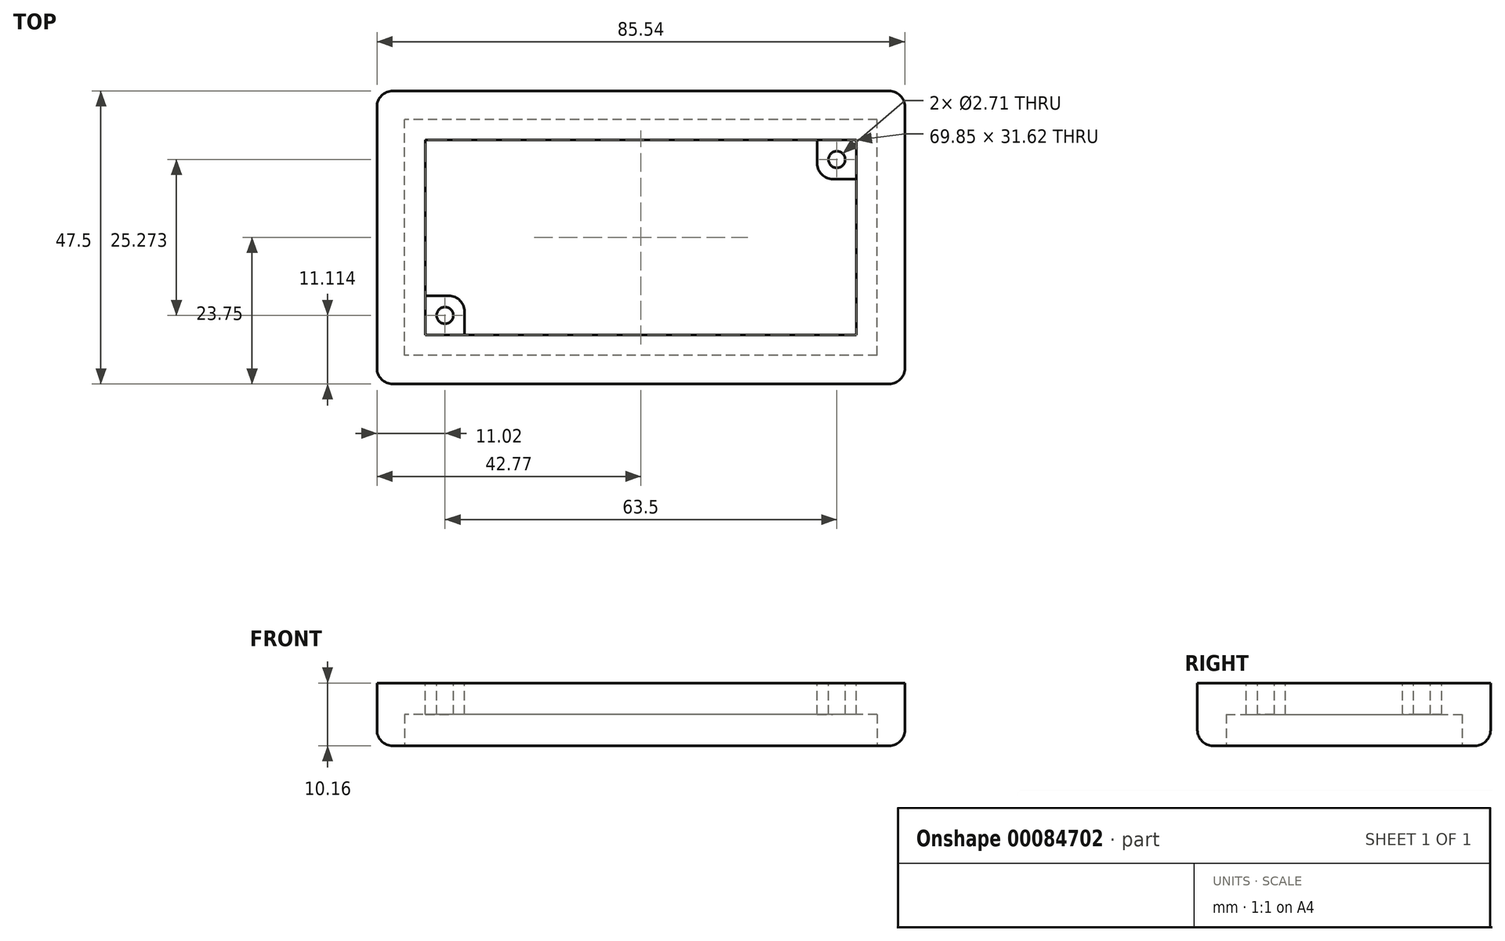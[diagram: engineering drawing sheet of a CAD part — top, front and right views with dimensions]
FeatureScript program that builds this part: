
annotation { "Feature Type Name" : "Feature", "Feature Type Description" : "" }
export const myFeature = defineFeature(function(context is Context, id is Id, definition is map)
    precondition{}
    {
        {
            var Q0;
            Q0=qCreatedBy(makeId("Top.planeOp"),FACE);
            var sketch = newSketch(context, id + "F0", { "sketchPlane" : qUnion([Q0])});
            skLineSegment(sketch, "E0.rect.bottom", {"start": v(34.93, -15.81) * mm, "end": v(-34.93, -15.81) * mm});
            skLineSegment(sketch, "E0.rect.top", {"start": v(34.93, 15.81) * mm, "end": v(-34.93, 15.81) * mm});
            skLineSegment(sketch, "E0.rect.left", {"start": v(34.93, -15.81) * mm, "end": v(34.93, 15.81) * mm});
            skLineSegment(sketch, "E0.rect.right", {"start": v(-34.93, -15.81) * mm, "end": v(-34.93, 15.81) * mm});
            skPoint(sketch, "E0.rect.middle", {"position": v(0, 0) * mm});
            skLineSegment(sketch, "E1.rect.bottom", {"start": v(42.77, -23.75) * mm, "end": v(-42.77, -23.75) * mm});
            skLineSegment(sketch, "E1.rect.top", {"start": v(42.77, 23.75) * mm, "end": v(-42.77, 23.75) * mm});
            skLineSegment(sketch, "E1.rect.left", {"start": v(42.77, -23.75) * mm, "end": v(42.77, 23.75) * mm});
            skLineSegment(sketch, "E1.rect.right", {"start": v(-42.77, -23.75) * mm, "end": v(-42.77, 23.75) * mm});
            skSolve(sketch);
        }
        {
            var Q0;
            Q0=makeQuery(id+"F0.imprint","IMPRINT",FACE,{"disambiguationData":[TD([[makeQuery(id+"F0.imprint","IMPRINT",EDGE,{"derivedFrom":sQuery(id+"F0.wireOp",EDGE,"E0.rect.bottom")}),1.0]])]});
            extrude(context, id + "F1", {"entities" : qUnion([Q0]), "depth" : 10.16 * mm});
        }
        {
            var Q0;
            Q0=makeQuery(id+"F1.opExtrude","CAP_FACE",FACE,{"disambiguationData":[OSD([sQuery(id+"F0.wireOp",EDGE,"E0.rect.bottom"),sQuery(id+"F0.wireOp",EDGE,"E0.rect.top"),sQuery(id+"F0.wireOp",EDGE,"E0.rect.left"),sQuery(id+"F0.wireOp",EDGE,"E0.rect.right"),sQuery(id+"F0.wireOp",EDGE,"E1.rect.bottom"),sQuery(id+"F0.wireOp",EDGE,"E1.rect.top"),sQuery(id+"F0.wireOp",EDGE,"E1.rect.left"),sQuery(id+"F0.wireOp",EDGE,"E1.rect.right")])],"isStart":false});
            var sketch = newSketch(context, id + "F2", { "sketchPlane" : qUnion([Q0])});
            skLineSegment(sketch, "E2.bottom", {"start": v(-34.93, -15.81) * mm, "end": v(-28.58, -15.81) * mm});
            skLineSegment(sketch, "E2.top", {"start": v(-34.93, -9.46) * mm, "end": v(-28.57, -9.46) * mm});
            skLineSegment(sketch, "E2.left", {"start": v(-34.93, -15.81) * mm, "end": v(-34.93, -9.46) * mm});
            skLineSegment(sketch, "E2.right", {"start": v(-28.58, -15.81) * mm, "end": v(-28.58, -9.46) * mm});
            skLineSegment(sketch, "E3.bottom", {"start": v(34.93, 15.81) * mm, "end": v(28.58, 15.81) * mm});
            skLineSegment(sketch, "E3.top", {"start": v(34.93, 9.46) * mm, "end": v(28.58, 9.46) * mm});
            skLineSegment(sketch, "E3.left", {"start": v(34.93, 15.81) * mm, "end": v(34.93, 9.46) * mm});
            skLineSegment(sketch, "E3.right", {"start": v(28.58, 15.81) * mm, "end": v(28.58, 9.46) * mm});
            skCircle(sketch, "E4", {"center": v(-31.75, -12.64) * mm, "radius": 1.35 * mm});
            skCircle(sketch, "E5", {"center": v(31.75, 12.64) * mm, "radius": 1.35 * mm});
            skSolve(sketch);
        }
        {
            var Q0;
            Q0=qSketchRegion(id+"F2",true);
            extrude(context, id + "F3", {"entities" : qUnion([Q0]), "oppositeDirection" : true, "depth" : 5.08 * mm});
        }
        {
            var Q0;
            Q0=makeQuery(id+"F3.opExtrude","SWEPT_EDGE",EDGE,{"disambiguationData":[OSD([sQuery(id+"F2.wireOp",EDGE,"E3.top"),sQuery(id+"F2.wireOp",EDGE,"E3.right")])]});
            var Q1;
            Q1=makeQuery(id+"F3.opExtrude","SWEPT_EDGE",EDGE,{"disambiguationData":[OSD([sQuery(id+"F2.wireOp",EDGE,"E2.top"),sQuery(id+"F2.wireOp",EDGE,"E2.right")])]});
            fillet(context, id + "F4", {"entities" : qUnion([Q0, Q1]), "radius" : 2.54 * mm, "tangentPropagation" : true, "allowEdgeOverflow" : false});
        }
        {
            var Q0;
            Q0=makeQuery(id+"F1.opExtrude","CAP_FACE",FACE,{"disambiguationData":[OSD([sQuery(id+"F0.wireOp",EDGE,"E0.rect.bottom"),sQuery(id+"F0.wireOp",EDGE,"E0.rect.top"),sQuery(id+"F0.wireOp",EDGE,"E0.rect.left"),sQuery(id+"F0.wireOp",EDGE,"E0.rect.right"),sQuery(id+"F0.wireOp",EDGE,"E1.rect.bottom"),sQuery(id+"F0.wireOp",EDGE,"E1.rect.top"),sQuery(id+"F0.wireOp",EDGE,"E1.rect.left"),sQuery(id+"F0.wireOp",EDGE,"E1.rect.right")])],"isStart":true});
            var sketch = newSketch(context, id + "F5", { "sketchPlane" : qUnion([Q0])});
            skLineSegment(sketch, "E6.rect.bottom", {"start": v(38.3, 19.11) * mm, "end": v(-38.3, 19.11) * mm});
            skLineSegment(sketch, "E6.rect.top", {"start": v(38.3, -19.11) * mm, "end": v(-38.3, -19.11) * mm});
            skLineSegment(sketch, "E6.rect.left", {"start": v(38.3, 19.11) * mm, "end": v(38.3, -19.11) * mm});
            skLineSegment(sketch, "E6.rect.right", {"start": v(-38.3, 19.11) * mm, "end": v(-38.3, -19.11) * mm});
            skPoint(sketch, "E6.rect.middle", {"position": v(0, 0) * mm});
            skSolve(sketch);
        }
        {
            var Q0;
            Q0=makeQuery(id+"F5.imprint","IMPRINT",FACE,{"disambiguationData":[TD([[makeQuery(id+"F5.imprint","IMPRINT",EDGE,{"derivedFrom":sQuery(id+"F5.wireOp",EDGE,"E6.rect.bottom")}),1.0]])]});
            extrude(context, id + "F6", {"entities" : qUnion([Q0]), "operationType" : NewBodyOperationType.REMOVE, "oppositeDirection" : true, "depth" : 5.08 * mm});
        }
        {
            var Q0;
            Q0=makeQuery(id+"F1.opExtrude","SWEPT_EDGE",EDGE,{"disambiguationData":[OSD([sQuery(id+"F0.wireOp",EDGE,"E1.rect.bottom"),sQuery(id+"F0.wireOp",EDGE,"E1.rect.left")])]});
            var Q1;
            Q1=makeQuery(id+"F1.opExtrude","SWEPT_EDGE",EDGE,{"disambiguationData":[OSD([sQuery(id+"F0.wireOp",EDGE,"E1.rect.top"),sQuery(id+"F0.wireOp",EDGE,"E1.rect.left")])]});
            var Q2;
            Q2=makeQuery(id+"F1.opExtrude","SWEPT_EDGE",EDGE,{"disambiguationData":[OSD([sQuery(id+"F0.wireOp",EDGE,"E1.rect.bottom"),sQuery(id+"F0.wireOp",EDGE,"E1.rect.right")])]});
            var Q3;
            Q3=makeQuery(id+"F1.opExtrude","SWEPT_EDGE",EDGE,{"disambiguationData":[OSD([sQuery(id+"F0.wireOp",EDGE,"E1.rect.top"),sQuery(id+"F0.wireOp",EDGE,"E1.rect.right")])]});
            var Q4;
            Q4=makeQuery(id+"F1.opExtrude","CAP_EDGE",EDGE,{"disambiguationData":[OSD([sQuery(id+"F0.wireOp",EDGE,"E1.rect.bottom")])],"isStart":true});
            var Q5;
            Q5=makeQuery(id+"F1.opExtrude","CAP_EDGE",EDGE,{"disambiguationData":[OSD([sQuery(id+"F0.wireOp",EDGE,"E1.rect.left")])],"isStart":true});
            var Q6;
            Q6=makeQuery(id+"F1.opExtrude","CAP_EDGE",EDGE,{"disambiguationData":[OSD([sQuery(id+"F0.wireOp",EDGE,"E1.rect.top")])],"isStart":true});
            var Q7;
            Q7=makeQuery(id+"F1.opExtrude","CAP_EDGE",EDGE,{"disambiguationData":[OSD([sQuery(id+"F0.wireOp",EDGE,"E1.rect.right")])],"isStart":true});
            fillet(context, id + "F7", {"entities" : qUnion([Q0, Q1, Q2, Q3, Q4, Q5, Q6, Q7]), "radius" : 2.54 * mm, "tangentPropagation" : true, "allowEdgeOverflow" : false});
        }
    });
